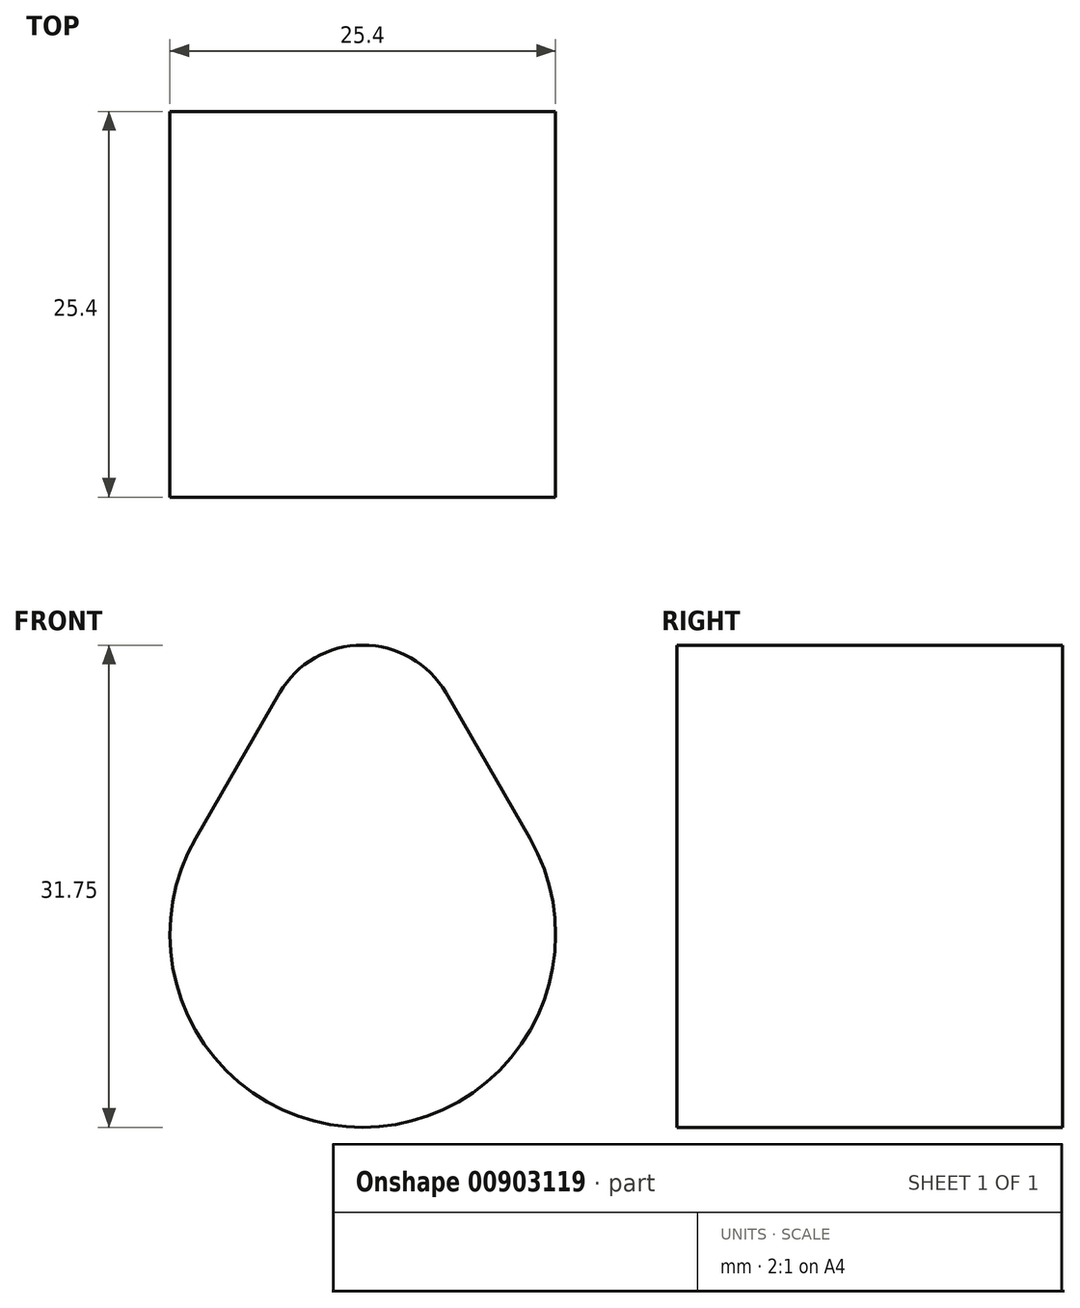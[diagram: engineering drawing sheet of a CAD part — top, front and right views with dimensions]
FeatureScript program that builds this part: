
annotation { "Feature Type Name" : "Feature", "Feature Type Description" : "" }
export const myFeature = defineFeature(function(context is Context, id is Id, definition is map)
    precondition{}
    {
        {
            var Q0;
            Q0=qCreatedBy(makeId("Front.planeOp"),FACE);
            var sketch = newSketch(context, id + "F0", { "sketchPlane" : qUnion([Q0])});
            skArc(sketch, "E0", {"start": v(-11, 6.35) * mm, "mid": v(0, -12.7) * mm, "end": v(11, 6.35) * mm});
            skArc(sketch, "E1", {"start": v(5.52, 15.84) * mm, "mid": v(0, 19.05) * mm, "end": v(-5.52, 15.84) * mm});
            skLineSegment(sketch, "E2", {"start": v(-5.48, 15.91) * mm, "end": v(-11, 6.35) * mm});
            skLineSegment(sketch, "E3", {"start": v(5.48, 15.91) * mm, "end": v(11, 6.35) * mm});
            skSolve(sketch);
        }
        {
            var Q0;
            {var subQ0=sQuery(id+"F0.wireOp",EDGE,"E0");Q0=makeQuery(id+"F0.imprint","IMPRINT",FACE,{"disambiguationData":[TD([[makeQuery(id+"F0.imprint","IMPRINT",EDGE,{"derivedFrom":subQ0}),1.0]])]});}
            extrude(context, id + "F1", {"entities" : qUnion([Q0]), "depth" : 25.4 * mm, "offsetDistance" : 25.4 * mm});
        }
    });
